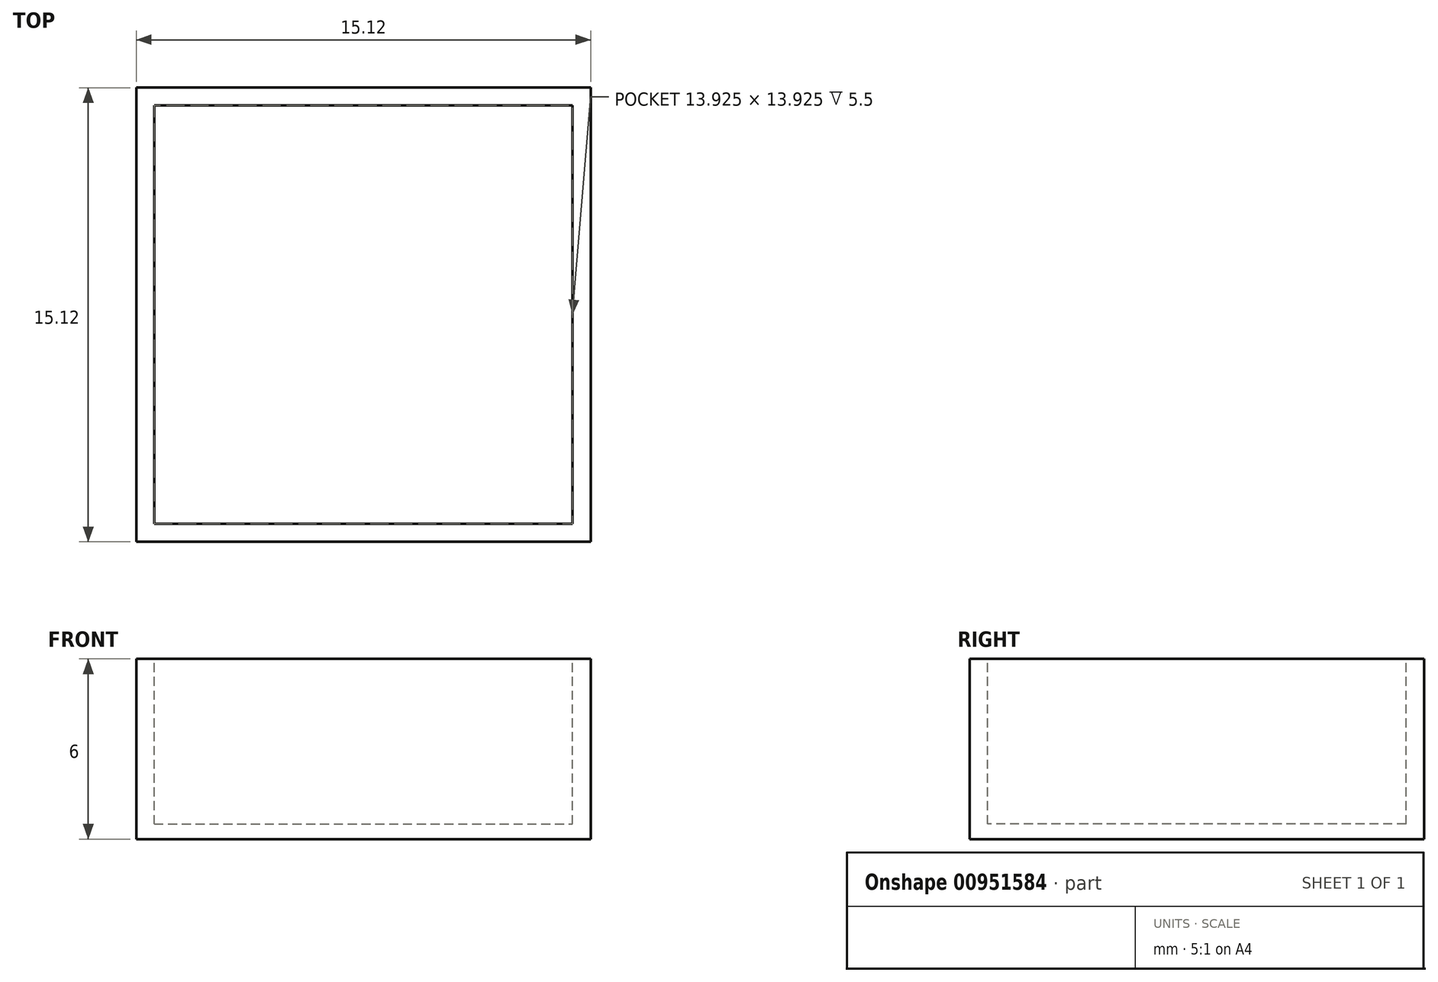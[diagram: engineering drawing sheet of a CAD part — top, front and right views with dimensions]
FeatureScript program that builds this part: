
annotation { "Feature Type Name" : "Feature", "Feature Type Description" : "" }
export const myFeature = defineFeature(function(context is Context, id is Id, definition is map)
    precondition{}
    {
        {
            var Q0;
            Q0=qCreatedBy(makeId("Top.planeOp"),FACE);
            var sketch = newSketch(context, id + "F0", { "sketchPlane" : qUnion([Q0])});
            skLineSegment(sketch, "E0.bottom", {"start": v(0, 0) * mm, "end": v(-15.13, 0) * mm});
            skLineSegment(sketch, "E0.top", {"start": v(0, 15.13) * mm, "end": v(-15.13, 15.13) * mm});
            skLineSegment(sketch, "E0.left", {"start": v(0, 0) * mm, "end": v(0, 15.13) * mm});
            skLineSegment(sketch, "E0.right", {"start": v(-15.13, 0) * mm, "end": v(-15.13, 15.13) * mm});
            skSolve(sketch);
        }
        {
            var Q0;
            Q0=makeQuery(id+"F0.imprint","IMPRINT",FACE,{"disambiguationData":[TD([[makeQuery(id+"F0.imprint","IMPRINT",EDGE,{"derivedFrom":sQuery(id+"F0.wireOp",EDGE,"E0.bottom")}),-1.0]])]});
            extrude(context, id + "F1", {"entities" : qUnion([Q0]), "depth" : 6 * mm, "offsetDistance" : 25 * mm});
        }
        {
            var Q0;
            Q0=makeQuery(id+"F1.opExtrude","CAP_FACE",FACE,{"disambiguationData":[OSD([sQuery(id+"F0.wireOp",EDGE,"E0.bottom"),sQuery(id+"F0.wireOp",EDGE,"E0.top"),sQuery(id+"F0.wireOp",EDGE,"E0.left"),sQuery(id+"F0.wireOp",EDGE,"E0.right")])],"isStart":false});
            var sketch = newSketch(context, id + "F2", { "sketchPlane" : qUnion([Q0])});
            skLineSegment(sketch, "E1", {"start": v(-15.13, 15.12) * mm, "end": v(0, 0) * mm});
            skSolve(sketch);
        }
        {
            var Q0;
            Q0=makeQuery(id+"F2.imprint","IMPRINT",FACE,{"disambiguationData":[TD([[makeQuery(id+"F2.imprint","IMPRINT",EDGE,{"derivedFrom":sQuery(id+"F2.wireOp",EDGE,"E1")}),-1.0]])]});
            var sketch = newSketch(context, id + "F3", { "sketchPlane" : qUnion([Q0])});
            skLineSegment(sketch, "E2.bottom", {"start": v(-14.53, 14.53) * mm, "end": v(-0.6, 14.53) * mm});
            skLineSegment(sketch, "E2.top", {"start": v(-14.53, 0.6) * mm, "end": v(-0.6, 0.6) * mm});
            skLineSegment(sketch, "E2.left", {"start": v(-14.53, 14.53) * mm, "end": v(-14.53, 0.6) * mm});
            skLineSegment(sketch, "E2.right", {"start": v(-0.6, 14.53) * mm, "end": v(-0.6, 0.6) * mm});
            skPoint(sketch, "E2.middle", {"position": v(-7.56, 7.56) * mm});
            skSolve(sketch);
        }
        {
            var Q0;
            Q0 = qSketchRegion(id + "F3", true);
            extrude(context, id + "F4", {"entities" : qUnion([Q0]), "operationType" : NewBodyOperationType.REMOVE, "oppositeDirection" : true, "depth" : (6 - .5) * mm, "offsetDistance" : 25 * mm});
        }
    });
